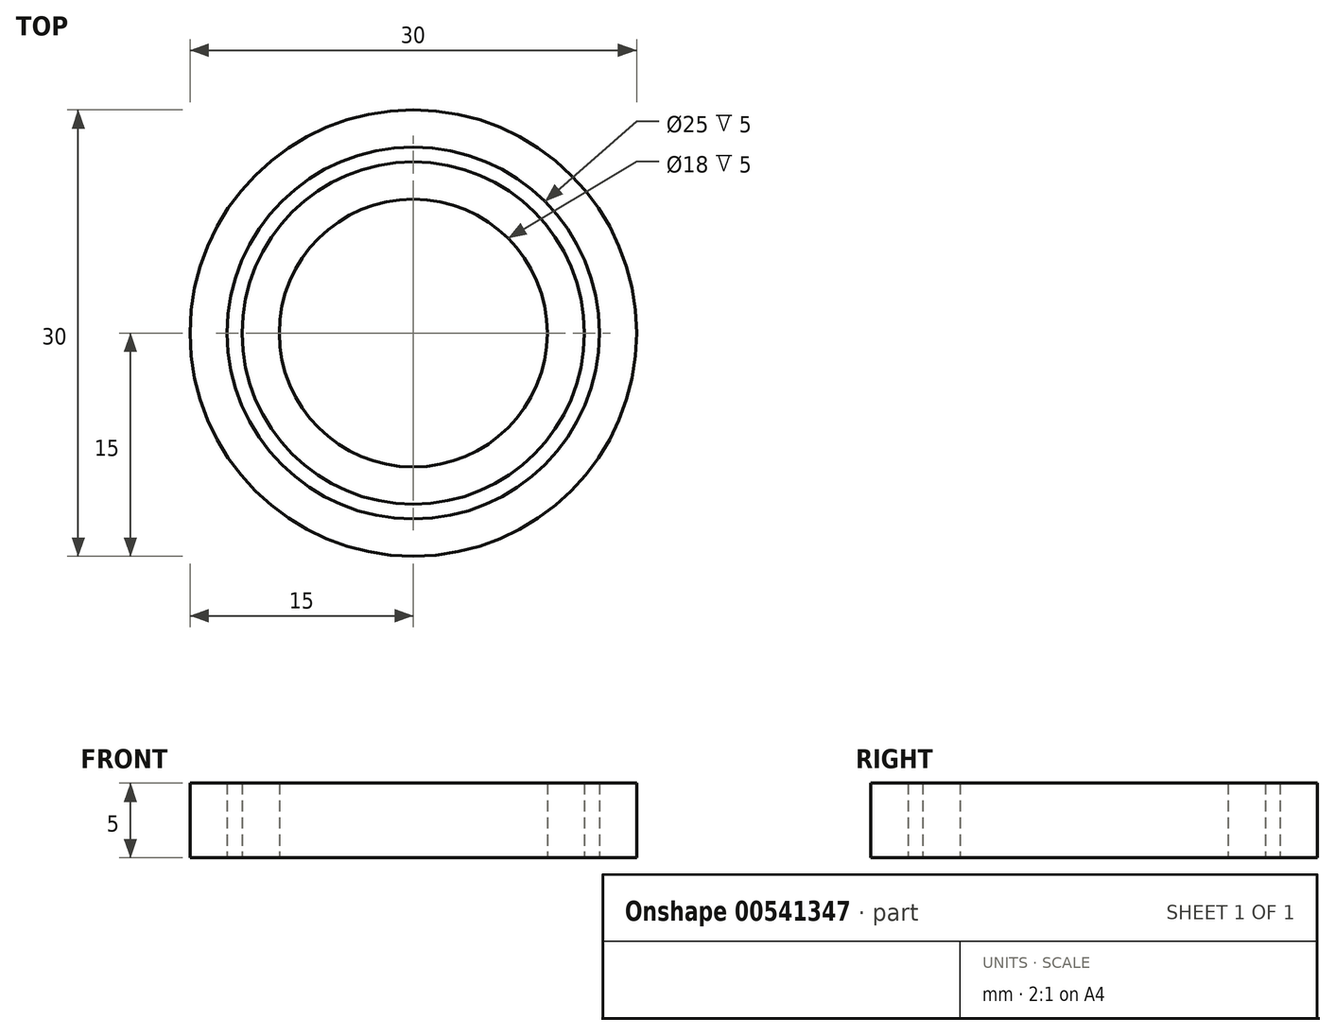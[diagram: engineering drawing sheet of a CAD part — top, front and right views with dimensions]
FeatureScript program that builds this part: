
annotation { "Feature Type Name" : "Feature", "Feature Type Description" : "" }
export const myFeature = defineFeature(function(context is Context, id is Id, definition is map)
    precondition{}
    {
        {
            var Q0;
            Q0=qCreatedBy(makeId("Top.planeOp"),FACE);
            var sketch = newSketch(context, id + "F0", { "sketchPlane" : qUnion([Q0])});
            skCircle(sketch, "E0", {"center": v(-10, 10) * mm, "radius": 12.5 * mm});
            skCircle(sketch, "E1", {"center": v(-10, 10) * mm, "radius": 15 * mm});
            skSolve(sketch);
        }
        {
            var Q0;
            Q0=qCreatedBy(makeId("Top.planeOp"),FACE);
            var sketch = newSketch(context, id + "F1", { "sketchPlane" : qUnion([Q0])});
            skCircle(sketch, "E2", {"center": v(-10, 10) * mm, "radius": 11.5 * mm});
            skCircle(sketch, "E3", {"center": v(-10, 10) * mm, "radius": 9 * mm});
            skSolve(sketch);
        }
        {
            var Q0;
            Q0 = qSketchRegion(id + "F0", true);
            extrude(context, id + "F2", {"entities" : qUnion([Q0]), "depth" : 5 * mm, "offsetDistance" : 25 * mm});
        }
        {
            var Q0;
            Q0 = qSketchRegion(id + "F1", true);
            extrude(context, id + "F3", {"entities" : qUnion([Q0]), "depth" : 5 * mm, "offsetDistance" : 25 * mm});
        }
    });
